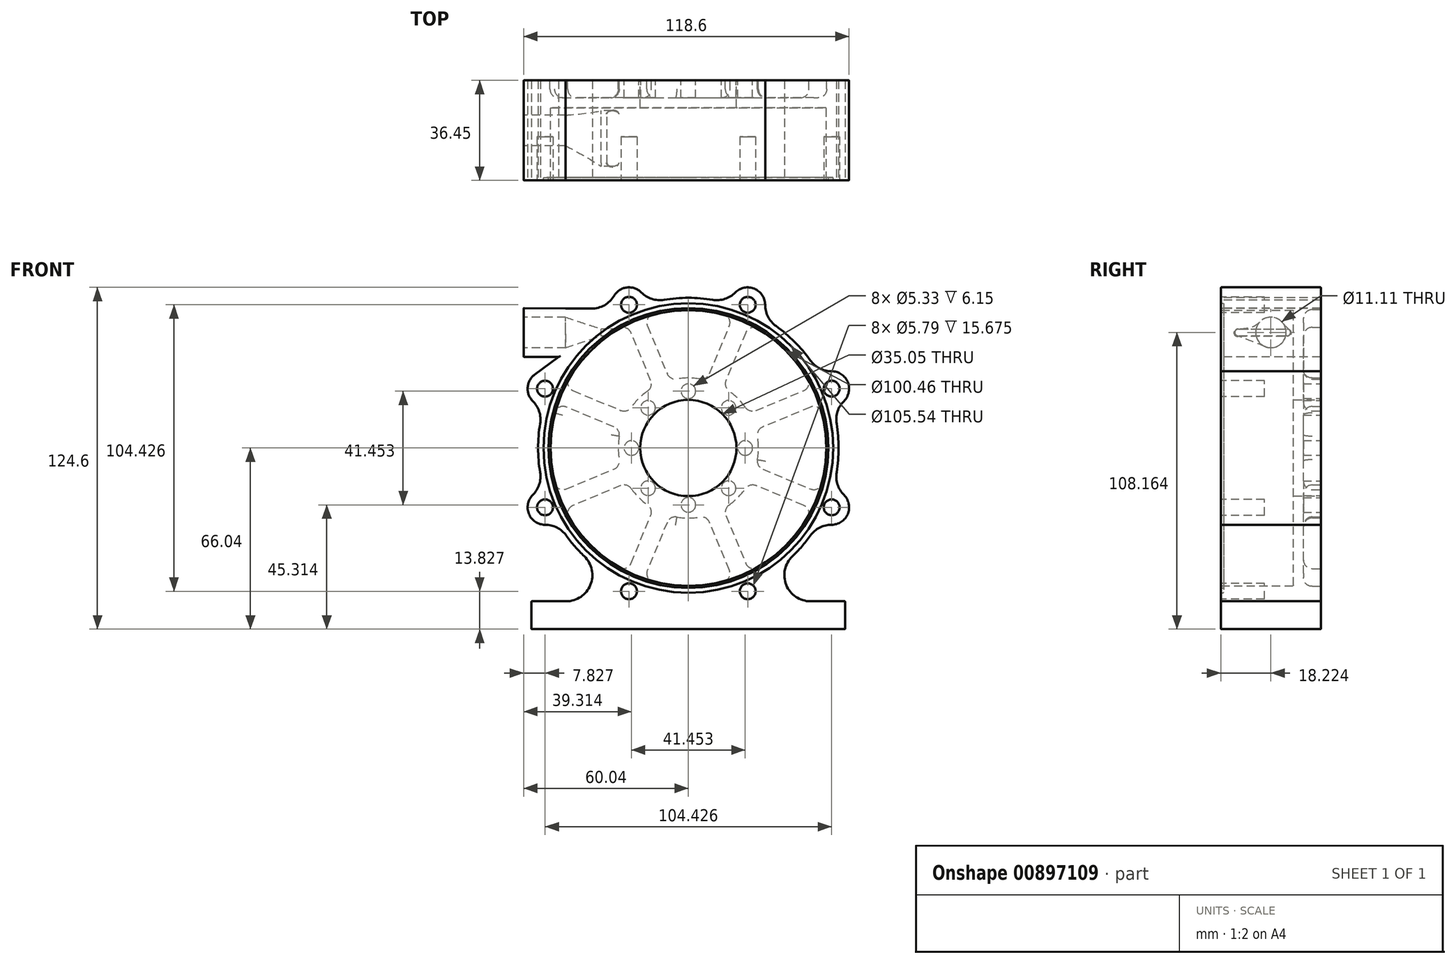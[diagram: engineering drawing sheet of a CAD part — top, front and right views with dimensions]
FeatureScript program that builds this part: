
annotation { "Feature Type Name" : "Feature", "Feature Type Description" : "" }
export const myFeature = defineFeature(function(context is Context, id is Id, definition is map)
    precondition{}
    {
        {
            var Q0;
            Q0=qCreatedBy(makeId("Front.planeOp"),FACE);
            var sketch = newSketch(context, id + "F0", { "sketchPlane" : qUnion([Q0])});
            skCircle(sketch, "E0", {"center": v(0, 0) * mm, "radius": 50.17 * mm, "construction": true});
            skArc(sketch, "E1", {"start": v(54.02, -8.84) * mm, "mid": v(54.74, 0) * mm, "end": v(54.02, 8.84) * mm});
            skCircle(sketch, "E2.cCircle", {"center": v(0, 0) * mm, "radius": 56.52 * mm, "construction": true});
            skLineSegment(sketch, "E2.0", {"start": v(52.21, -21.63) * mm, "end": v(21.63, -52.21) * mm, "construction": true});
            skLineSegment(sketch, "E2.1", {"start": v(21.63, -52.21) * mm, "end": v(-21.63, -52.21) * mm, "construction": true});
            skLineSegment(sketch, "E2.2", {"start": v(-21.63, -52.21) * mm, "end": v(-52.21, -21.63) * mm, "construction": true});
            skLineSegment(sketch, "E2.3", {"start": v(-52.21, -21.63) * mm, "end": v(-52.21, 21.63) * mm, "construction": true});
            skLineSegment(sketch, "E2.4", {"start": v(-52.21, 21.63) * mm, "end": v(-21.63, 52.21) * mm, "construction": true});
            skLineSegment(sketch, "E2.5", {"start": v(-21.63, 52.21) * mm, "end": v(21.63, 52.21) * mm, "construction": true});
            skLineSegment(sketch, "E2.6", {"start": v(21.63, 52.21) * mm, "end": v(52.21, 21.63) * mm, "construction": true});
            skLineSegment(sketch, "E2.7", {"start": v(52.21, 21.63) * mm, "end": v(52.21, -21.63) * mm, "construction": true});
            skArc(sketch, "E3", {"start": v(27.98, 52.2) * mm, "mid": v(24.06, 58.08) * mm, "end": v(17.13, 56.7) * mm});
            skArc(sketch, "E4", {"start": v(56.7, 17.13) * mm, "mid": v(58.08, 24.06) * mm, "end": v(52.2, 27.98) * mm});
            skArc(sketch, "E5", {"start": v(52.2, -27.98) * mm, "mid": v(58.08, -24.06) * mm, "end": v(56.7, -17.13) * mm});
            skArc(sketch, "E6", {"start": v(-56.7, -17.13) * mm, "mid": v(-58.08, -24.06) * mm, "end": v(-52.2, -27.98) * mm});
            skArc(sketch, "E7", {"start": v(-56, 26.73) * mm, "mid": v(-58.55, 22.09) * mm, "end": v(-56.7, 17.13) * mm});
            skArc(sketch, "E8.trimOffspring", {"start": v(44.45, 31.94) * mm, "mid": v(38.7, 38.7) * mm, "end": v(31.94, 44.45) * mm});
            skArc(sketch, "E9.trimOffspring", {"start": v(8.84, 54.02) * mm, "mid": v(0, 54.74) * mm, "end": v(-8.84, 54.02) * mm});
            skArc(sketch, "E10.trimOffspring", {"start": v(-54.02, 8.84) * mm, "mid": v(-54.74, 0) * mm, "end": v(-54.02, -8.84) * mm});
            skArc(sketch, "E11.trimOffspring", {"start": v(-44.45, -31.94) * mm, "mid": v(-41.35, -35.86) * mm, "end": v(-37.9, -39.48) * mm});
            skArc(sketch, "E12.trimOffspring", {"start": v(37.9, -39.48) * mm, "mid": v(41.35, -35.86) * mm, "end": v(44.45, -31.94) * mm});
            skLineSegment(sketch, "E13", {"start": v(-57.15, -55.88) * mm, "end": v(-57.15, -66.04) * mm});
            skLineSegment(sketch, "E14", {"start": v(-57.15, -66.04) * mm, "end": v(57.15, -66.04) * mm});
            skLineSegment(sketch, "E15", {"start": v(57.15, -66.04) * mm, "end": v(57.15, -55.88) * mm});
            skLineSegment(sketch, "E16", {"start": v(57.15, -55.88) * mm, "end": v(44.5, -55.88) * mm});
            skLineSegment(sketch, "E17", {"start": v(-57.15, -55.88) * mm, "end": v(-44.5, -55.88) * mm});
            skPoint(sketch, "E18", {"position": v(0, -66.04) * mm});
            skArc(sketch, "E19", {"start": v(-44.5, -55.88) * mm, "mid": v(-35.67, -49.91) * mm, "end": v(-37.9, -39.48) * mm});
            skArc(sketch, "E20", {"start": v(37.9, -39.48) * mm, "mid": v(35.67, -49.91) * mm, "end": v(44.5, -55.88) * mm});
            skPoint(sketch, "E21.visualSharp", {"position": v(-47.97, -26.36) * mm});
            skArc(sketch, "E21.filletArc", {"start": v(-44.45, -31.94) * mm, "mid": v(-47.85, -29.02) * mm, "end": v(-52.2, -27.98) * mm});
            skPoint(sketch, "E22.visualSharp", {"position": v(-52.56, -15.29) * mm});
            skArc(sketch, "E22.filletArc", {"start": v(-56.7, -17.13) * mm, "mid": v(-54.35, -13.3) * mm, "end": v(-54.02, -8.84) * mm});
            skPoint(sketch, "E23.visualSharp", {"position": v(-52.56, 15.29) * mm});
            skArc(sketch, "E23.filletArc", {"start": v(-54.02, 8.84) * mm, "mid": v(-54.35, 13.3) * mm, "end": v(-56.7, 17.13) * mm});
            skPoint(sketch, "E24.visualSharp", {"position": v(47.97, -26.36) * mm});
            skArc(sketch, "E24.filletArc", {"start": v(52.2, -27.98) * mm, "mid": v(47.85, -29.02) * mm, "end": v(44.45, -31.94) * mm});
            skPoint(sketch, "E25.visualSharp", {"position": v(52.56, -15.29) * mm});
            skArc(sketch, "E25.filletArc", {"start": v(54.02, -8.84) * mm, "mid": v(54.35, -13.3) * mm, "end": v(56.7, -17.13) * mm});
            skPoint(sketch, "E26.visualSharp", {"position": v(52.56, 15.29) * mm});
            skArc(sketch, "E26.filletArc", {"start": v(56.7, 17.13) * mm, "mid": v(54.35, 13.3) * mm, "end": v(54.02, 8.84) * mm});
            skPoint(sketch, "E27.visualSharp", {"position": v(47.97, 26.36) * mm});
            skArc(sketch, "E27.filletArc", {"start": v(44.45, 31.94) * mm, "mid": v(47.85, 29.02) * mm, "end": v(52.2, 27.98) * mm});
            skPoint(sketch, "E28.visualSharp", {"position": v(26.36, 47.97) * mm});
            skArc(sketch, "E28.filletArc", {"start": v(27.98, 52.2) * mm, "mid": v(29.02, 47.85) * mm, "end": v(31.94, 44.45) * mm});
            skPoint(sketch, "E29.visualSharp", {"position": v(15.29, 52.56) * mm});
            skArc(sketch, "E29.filletArc", {"start": v(8.84, 54.02) * mm, "mid": v(13.3, 54.35) * mm, "end": v(17.13, 56.7) * mm});
            skPoint(sketch, "E30.visualSharp", {"position": v(-15.29, 52.56) * mm});
            skLineSegment(sketch, "E31", {"start": v(-35.27, 50.8) * mm, "end": v(-44.8, 50.8) * mm});
            skArc(sketch, "E32", {"start": v(-17.13, 56.7) * mm, "mid": v(-22.41, 58.51) * mm, "end": v(-27.09, 55.46) * mm});
            skArc(sketch, "E33.filletArc", {"start": v(-17.13, 56.7) * mm, "mid": v(-13.3, 54.35) * mm, "end": v(-8.84, 54.02) * mm});
            skPoint(sketch, "E34.visualSharp", {"position": v(-27.82, 50.8) * mm});
            skArc(sketch, "E34.filletArc", {"start": v(-35.27, 50.8) * mm, "mid": v(-30.56, 52.05) * mm, "end": v(-27.09, 55.46) * mm});
            skLineSegment(sketch, "E35", {"start": v(-47.22, 33.23) * mm, "end": v(-56, 26.73) * mm});
            skLineSegment(sketch, "E36", {"start": v(-44.8, 50.8) * mm, "end": v(-60.04, 51.01) * mm});
            skLineSegment(sketch, "E37", {"start": v(-60.04, 51.01) * mm, "end": v(-60.04, 33.23) * mm});
            skLineSegment(sketch, "E38", {"start": v(-60.04, 33.23) * mm, "end": v(-47.22, 33.23) * mm});
            skSolve(sketch);
        }
        {
            var Q0;
            Q0=qSketchRegion(id+"F0",true);
            extrude(context, id + "F1", {"entities" : qUnion([Q0]), "oppositeDirection" : true, "depth" : 36.45 * mm});
        }
        {
            var Q0;
            Q0=qCreatedBy(makeId("Right.planeOp"),FACE);
            var sketch = newSketch(context, id + "F2", { "sketchPlane" : qUnion([Q0])});
            skLineSegment(sketch, "E39", {"start": v(0, 0) * mm, "end": v(0, 50.23) * mm});
            skLineSegment(sketch, "E40", {"start": v(26.42, 50.23) * mm, "end": v(0, 50.23) * mm});
            skLineSegment(sketch, "E41", {"start": v(26.42, 50.23) * mm, "end": v(26.42, 17.53) * mm});
            skLineSegment(sketch, "E42", {"start": v(36.45, 17.53) * mm, "end": v(26.42, 17.53) * mm});
            skLineSegment(sketch, "E43", {"start": v(36.45, 17.53) * mm, "end": v(36.45, 0) * mm});
            skLineSegment(sketch, "E44", {"start": v(0, 0) * mm, "end": v(36.45, 0) * mm});
            skLineSegment(sketch, "E45.bottom", {"start": v(1.02, 51) * mm, "end": v(0, 51) * mm});
            skLineSegment(sketch, "E45.top", {"start": v(1.02, 52.77) * mm, "end": v(0, 52.77) * mm});
            skLineSegment(sketch, "E45.left", {"start": v(0, 51) * mm, "end": v(0, 52.77) * mm});
            skLineSegment(sketch, "E45.right", {"start": v(1.02, 51) * mm, "end": v(1.02, 52.77) * mm});
            skSolve(sketch);
        }
        {
            var Q0;
            Q0=qSketchRegion(id+"F2",true);
            var Q1;
            Q1=sQuery(id+"F2.wireOp",EDGE,"E44");
            revolve(context, id + "F3", {"operationType" : NewBodyOperationType.REMOVE, "entities" : qUnion([Q0]), "axis" : qUnion([Q1]), "revolveType" : RevolveType.FULL, "oppositeDirection" : true});
        }
        {
            var Q0;
            Q0=makeQuery(id+"F1.opExtrude","CAP_FACE",FACE,{"disambiguationData":[OSD([sQuery(id+"F0.wireOp",EDGE,"E1"),sQuery(id+"F0.wireOp",EDGE,"E3"),sQuery(id+"F0.wireOp",EDGE,"E4"),sQuery(id+"F0.wireOp",EDGE,"E5"),sQuery(id+"F0.wireOp",EDGE,"E6"),sQuery(id+"F0.wireOp",EDGE,"E7"),sQuery(id+"F0.wireOp",EDGE,"E8.trimOffspring"),sQuery(id+"F0.wireOp",EDGE,"E9.trimOffspring"),sQuery(id+"F0.wireOp",EDGE,"E10.trimOffspring"),sQuery(id+"F0.wireOp",EDGE,"E11.trimOffspring"),sQuery(id+"F0.wireOp",EDGE,"E12.trimOffspring"),sQuery(id+"F0.wireOp",EDGE,"E13"),sQuery(id+"F0.wireOp",EDGE,"E14"),sQuery(id+"F0.wireOp",EDGE,"E15"),sQuery(id+"F0.wireOp",EDGE,"E16"),sQuery(id+"F0.wireOp",EDGE,"E17"),sQuery(id+"F0.wireOp",EDGE,"E19"),sQuery(id+"F0.wireOp",EDGE,"E20"),sQuery(id+"F0.wireOp",EDGE,"E21.filletArc"),sQuery(id+"F0.wireOp",EDGE,"E22.filletArc"),sQuery(id+"F0.wireOp",EDGE,"E23.filletArc"),sQuery(id+"F0.wireOp",EDGE,"E24.filletArc"),sQuery(id+"F0.wireOp",EDGE,"E25.filletArc"),sQuery(id+"F0.wireOp",EDGE,"E26.filletArc"),sQuery(id+"F0.wireOp",EDGE,"E27.filletArc"),sQuery(id+"F0.wireOp",EDGE,"E28.filletArc"),sQuery(id+"F0.wireOp",EDGE,"E29.filletArc"),sQuery(id+"F0.wireOp",EDGE,"E31"),sQuery(id+"F0.wireOp",EDGE,"kHr8fFUD-4EFk-nJZE-7JVT-0WPmz8yTTr2E"),sQuery(id+"F0.wireOp",EDGE,"E32"),sQuery(id+"F0.wireOp",EDGE,"E33.filletArc"),sQuery(id+"F0.wireOp",EDGE,"E34.filletArc"),sQuery(id+"F0.wireOp",EDGE,"fBgQRkSS-CIUt-JJdx-RIVp-XrYWp9c1mPRc"),sQuery(id+"F0.wireOp",EDGE,"E35")])],"isStart":false});
            var sketch = newSketch(context, id + "F4", { "sketchPlane" : qUnion([Q0])});
            skPoint(sketch, "E46.center", {"position": v(0, 0) * mm});
            skArc(sketch, "E47", {"start": v(4.25, 25.17) * mm, "mid": v(0, 25.53) * mm, "end": v(-4.25, 25.17) * mm});
            skLineSegment(sketch, "E48", {"start": v(0, 0) * mm, "end": v(24.06, 58.08) * mm, "construction": true});
            skLineSegment(sketch, "E49", {"start": v(0, 0) * mm, "end": v(0, 17.53) * mm, "construction": true});
            skArc(sketch, "E50", {"start": v(12.8, 48.77) * mm, "mid": v(0, 50.42) * mm, "end": v(-12.8, 48.77) * mm});
            skLineSegment(sketch, "E51", {"start": v(14.92, 44.48) * mm, "end": v(7.71, 27.09) * mm});
            skLineSegment(sketch, "E52", {"start": v(-7.71, 27.09) * mm, "end": v(-14.92, 44.48) * mm});
            skPoint(sketch, "E53.visualSharp", {"position": v(-16.26, 47.72) * mm});
            skArc(sketch, "E53.filletArc", {"start": v(-12.8, 48.77) * mm, "mid": v(-14.83, 47.1) * mm, "end": v(-14.92, 44.48) * mm});
            skPoint(sketch, "E54.visualSharp", {"position": v(16.26, 47.72) * mm});
            skArc(sketch, "E54.filletArc", {"start": v(14.92, 44.48) * mm, "mid": v(14.83, 47.1) * mm, "end": v(12.8, 48.77) * mm});
            skPoint(sketch, "E55.visualSharp", {"position": v(6.7, 24.63) * mm});
            skArc(sketch, "E55.filletArc", {"start": v(4.25, 25.17) * mm, "mid": v(6.32, 25.52) * mm, "end": v(7.71, 27.09) * mm});
            skPoint(sketch, "E56.visualSharp", {"position": v(-6.7, 24.63) * mm});
            skArc(sketch, "E56.filletArc", {"start": v(-7.71, 27.09) * mm, "mid": v(-6.32, 25.52) * mm, "end": v(-4.25, 25.17) * mm});
            skArc(sketch, "E57.1.0", {"start": v(-43.53, 25.44) * mm, "mid": v(-43.8, 22.82) * mm, "end": v(-42, 20.9) * mm});
            skLineSegment(sketch, "E57.1.1", {"start": v(-24.6, 13.7) * mm, "end": v(-42, 20.9) * mm});
            skArc(sketch, "E57.1.2", {"start": v(-14.8, 20.8) * mm, "mid": v(-18.05, 18.05) * mm, "end": v(-20.8, 14.8) * mm});
            skArc(sketch, "E57.1.3", {"start": v(-24.6, 13.7) * mm, "mid": v(-22.51, 13.58) * mm, "end": v(-20.8, 14.8) * mm});
            skArc(sketch, "E57.1.4", {"start": v(-14.8, 20.8) * mm, "mid": v(-13.58, 22.51) * mm, "end": v(-13.7, 24.6) * mm});
            skLineSegment(sketch, "E57.1.5", {"start": v(-20.9, 42) * mm, "end": v(-13.7, 24.6) * mm});
            skArc(sketch, "E57.1.6", {"start": v(-20.9, 42) * mm, "mid": v(-22.82, 43.8) * mm, "end": v(-25.44, 43.53) * mm});
            skArc(sketch, "E57.1.7", {"start": v(-25.44, 43.53) * mm, "mid": v(-35.65, 35.65) * mm, "end": v(-43.53, 25.44) * mm});
            skArc(sketch, "E57.2.0", {"start": v(-48.77, -12.8) * mm, "mid": v(-47.1, -14.83) * mm, "end": v(-44.48, -14.92) * mm});
            skLineSegment(sketch, "E57.2.1", {"start": v(-27.09, -7.71) * mm, "end": v(-44.48, -14.92) * mm});
            skArc(sketch, "E57.2.2", {"start": v(-25.17, 4.25) * mm, "mid": v(-25.53, 0) * mm, "end": v(-25.17, -4.25) * mm});
            skArc(sketch, "E57.2.3", {"start": v(-27.09, -7.71) * mm, "mid": v(-25.52, -6.32) * mm, "end": v(-25.17, -4.25) * mm});
            skArc(sketch, "E57.2.4", {"start": v(-25.17, 4.25) * mm, "mid": v(-25.52, 6.32) * mm, "end": v(-27.09, 7.71) * mm});
            skLineSegment(sketch, "E57.2.5", {"start": v(-44.48, 14.92) * mm, "end": v(-27.09, 7.71) * mm});
            skArc(sketch, "E57.2.6", {"start": v(-44.48, 14.92) * mm, "mid": v(-47.1, 14.83) * mm, "end": v(-48.77, 12.8) * mm});
            skArc(sketch, "E57.2.7", {"start": v(-48.77, 12.8) * mm, "mid": v(-50.42, 0) * mm, "end": v(-48.77, -12.8) * mm});
            skArc(sketch, "E57.3.0", {"start": v(-25.44, -43.53) * mm, "mid": v(-22.82, -43.8) * mm, "end": v(-20.9, -42) * mm});
            skLineSegment(sketch, "E57.3.1", {"start": v(-13.7, -24.6) * mm, "end": v(-20.9, -42) * mm});
            skArc(sketch, "E57.3.2", {"start": v(-20.8, -14.8) * mm, "mid": v(-18.05, -18.05) * mm, "end": v(-14.8, -20.8) * mm});
            skArc(sketch, "E57.3.3", {"start": v(-13.7, -24.6) * mm, "mid": v(-13.58, -22.51) * mm, "end": v(-14.8, -20.8) * mm});
            skArc(sketch, "E57.3.4", {"start": v(-20.8, -14.8) * mm, "mid": v(-22.51, -13.58) * mm, "end": v(-24.6, -13.7) * mm});
            skLineSegment(sketch, "E57.3.5", {"start": v(-42, -20.9) * mm, "end": v(-24.6, -13.7) * mm});
            skArc(sketch, "E57.3.6", {"start": v(-42, -20.9) * mm, "mid": v(-43.8, -22.82) * mm, "end": v(-43.53, -25.44) * mm});
            skArc(sketch, "E57.3.7", {"start": v(-43.53, -25.44) * mm, "mid": v(-35.65, -35.65) * mm, "end": v(-25.44, -43.53) * mm});
            skArc(sketch, "E57.4.0", {"start": v(12.8, -48.77) * mm, "mid": v(14.83, -47.1) * mm, "end": v(14.92, -44.48) * mm});
            skLineSegment(sketch, "E57.4.1", {"start": v(7.71, -27.09) * mm, "end": v(14.92, -44.48) * mm});
            skArc(sketch, "E57.4.2", {"start": v(-4.25, -25.17) * mm, "mid": v(0, -25.53) * mm, "end": v(4.25, -25.17) * mm});
            skArc(sketch, "E57.4.3", {"start": v(7.71, -27.09) * mm, "mid": v(6.32, -25.52) * mm, "end": v(4.25, -25.17) * mm});
            skArc(sketch, "E57.4.4", {"start": v(-4.25, -25.17) * mm, "mid": v(-6.32, -25.52) * mm, "end": v(-7.71, -27.09) * mm});
            skLineSegment(sketch, "E57.4.5", {"start": v(-14.92, -44.48) * mm, "end": v(-7.71, -27.09) * mm});
            skArc(sketch, "E57.4.6", {"start": v(-14.92, -44.48) * mm, "mid": v(-14.83, -47.1) * mm, "end": v(-12.8, -48.77) * mm});
            skArc(sketch, "E57.4.7", {"start": v(-12.8, -48.77) * mm, "mid": v(0, -50.42) * mm, "end": v(12.8, -48.77) * mm});
            skArc(sketch, "E57.5.0", {"start": v(43.53, -25.44) * mm, "mid": v(43.8, -22.82) * mm, "end": v(42, -20.9) * mm});
            skLineSegment(sketch, "E57.5.1", {"start": v(24.6, -13.7) * mm, "end": v(42, -20.9) * mm});
            skArc(sketch, "E57.5.2", {"start": v(14.8, -20.8) * mm, "mid": v(18.05, -18.05) * mm, "end": v(20.8, -14.8) * mm});
            skArc(sketch, "E57.5.3", {"start": v(24.6, -13.7) * mm, "mid": v(22.51, -13.58) * mm, "end": v(20.8, -14.8) * mm});
            skArc(sketch, "E57.5.4", {"start": v(14.8, -20.8) * mm, "mid": v(13.58, -22.51) * mm, "end": v(13.7, -24.6) * mm});
            skLineSegment(sketch, "E57.5.5", {"start": v(20.9, -42) * mm, "end": v(13.7, -24.6) * mm});
            skArc(sketch, "E57.5.6", {"start": v(20.9, -42) * mm, "mid": v(22.82, -43.8) * mm, "end": v(25.44, -43.53) * mm});
            skArc(sketch, "E57.5.7", {"start": v(25.44, -43.53) * mm, "mid": v(35.65, -35.65) * mm, "end": v(43.53, -25.44) * mm});
            skArc(sketch, "E57.6.0", {"start": v(48.77, 12.8) * mm, "mid": v(47.1, 14.83) * mm, "end": v(44.48, 14.92) * mm});
            skLineSegment(sketch, "E57.6.1", {"start": v(27.09, 7.71) * mm, "end": v(44.48, 14.92) * mm});
            skArc(sketch, "E57.6.2", {"start": v(25.17, -4.25) * mm, "mid": v(25.53, 0) * mm, "end": v(25.17, 4.25) * mm});
            skArc(sketch, "E57.6.3", {"start": v(27.09, 7.71) * mm, "mid": v(25.52, 6.32) * mm, "end": v(25.17, 4.25) * mm});
            skArc(sketch, "E57.6.4", {"start": v(25.17, -4.25) * mm, "mid": v(25.52, -6.32) * mm, "end": v(27.09, -7.71) * mm});
            skLineSegment(sketch, "E57.6.5", {"start": v(44.48, -14.92) * mm, "end": v(27.09, -7.71) * mm});
            skArc(sketch, "E57.6.6", {"start": v(44.48, -14.92) * mm, "mid": v(47.1, -14.83) * mm, "end": v(48.77, -12.8) * mm});
            skArc(sketch, "E57.6.7", {"start": v(48.77, -12.8) * mm, "mid": v(50.42, 0) * mm, "end": v(48.77, 12.8) * mm});
            skArc(sketch, "E57.7.0", {"start": v(25.44, 43.53) * mm, "mid": v(22.82, 43.8) * mm, "end": v(20.9, 42) * mm});
            skLineSegment(sketch, "E57.7.1", {"start": v(13.7, 24.6) * mm, "end": v(20.9, 42) * mm});
            skArc(sketch, "E57.7.2", {"start": v(20.8, 14.8) * mm, "mid": v(18.05, 18.05) * mm, "end": v(14.8, 20.8) * mm});
            skArc(sketch, "E57.7.3", {"start": v(13.7, 24.6) * mm, "mid": v(13.58, 22.51) * mm, "end": v(14.8, 20.8) * mm});
            skArc(sketch, "E57.7.4", {"start": v(20.8, 14.8) * mm, "mid": v(22.51, 13.58) * mm, "end": v(24.6, 13.7) * mm});
            skLineSegment(sketch, "E57.7.5", {"start": v(42, 20.9) * mm, "end": v(24.6, 13.7) * mm});
            skArc(sketch, "E57.7.6", {"start": v(42, 20.9) * mm, "mid": v(43.8, 22.82) * mm, "end": v(43.53, 25.44) * mm});
            skArc(sketch, "E57.7.7", {"start": v(43.53, 25.44) * mm, "mid": v(35.65, 35.65) * mm, "end": v(25.44, 43.53) * mm});
            skSolve(sketch);
        }
        {
            var Q0;
            Q0=qSketchRegion(id+"F4",true);
            extrude(context, id + "F5", {"entities" : qUnion([Q0]), "operationType" : NewBodyOperationType.REMOVE, "oppositeDirection" : true, "depth" : 6.35 * mm});
        }
        {
            var Q0;
            Q0=makeQuery(id+"F5.boolean.opBoolean","COPY",FACE,{"derivedFrom":makeQuery(id+"F5.opExtrude","CAP_FACE",FACE,{"disambiguationData":[OSD([sQuery(id+"F4.wireOp",EDGE,"E47"),sQuery(id+"F4.wireOp",EDGE,"E50"),sQuery(id+"F4.wireOp",EDGE,"E51"),sQuery(id+"F4.wireOp",EDGE,"E52"),sQuery(id+"F4.wireOp",EDGE,"E53.filletArc"),sQuery(id+"F4.wireOp",EDGE,"E54.filletArc"),sQuery(id+"F4.wireOp",EDGE,"E55.filletArc"),sQuery(id+"F4.wireOp",EDGE,"E56.filletArc")])],"isStart":false})});
            var Q1;
            Q1=makeQuery(id+"F5.boolean.opBoolean","COPY",FACE,{"derivedFrom":makeQuery(id+"F5.opExtrude","CAP_FACE",FACE,{"disambiguationData":[OSD([sQuery(id+"F4.wireOp",EDGE,"E57.7.0"),sQuery(id+"F4.wireOp",EDGE,"E57.7.1"),sQuery(id+"F4.wireOp",EDGE,"E57.7.2"),sQuery(id+"F4.wireOp",EDGE,"E57.7.3"),sQuery(id+"F4.wireOp",EDGE,"E57.7.4"),sQuery(id+"F4.wireOp",EDGE,"E57.7.5"),sQuery(id+"F4.wireOp",EDGE,"E57.7.6"),sQuery(id+"F4.wireOp",EDGE,"E57.7.7")])],"isStart":false})});
            var Q2;
            Q2=makeQuery(id+"F5.boolean.opBoolean","COPY",FACE,{"derivedFrom":makeQuery(id+"F5.opExtrude","CAP_FACE",FACE,{"disambiguationData":[OSD([sQuery(id+"F4.wireOp",EDGE,"E57.6.0"),sQuery(id+"F4.wireOp",EDGE,"E57.6.1"),sQuery(id+"F4.wireOp",EDGE,"E57.6.2"),sQuery(id+"F4.wireOp",EDGE,"E57.6.3"),sQuery(id+"F4.wireOp",EDGE,"E57.6.4"),sQuery(id+"F4.wireOp",EDGE,"E57.6.5"),sQuery(id+"F4.wireOp",EDGE,"E57.6.6"),sQuery(id+"F4.wireOp",EDGE,"E57.6.7")])],"isStart":false})});
            var Q3;
            Q3=makeQuery(id+"F5.boolean.opBoolean","COPY",FACE,{"derivedFrom":makeQuery(id+"F5.opExtrude","CAP_FACE",FACE,{"disambiguationData":[OSD([sQuery(id+"F4.wireOp",EDGE,"E57.5.0"),sQuery(id+"F4.wireOp",EDGE,"E57.5.1"),sQuery(id+"F4.wireOp",EDGE,"E57.5.2"),sQuery(id+"F4.wireOp",EDGE,"E57.5.3"),sQuery(id+"F4.wireOp",EDGE,"E57.5.4"),sQuery(id+"F4.wireOp",EDGE,"E57.5.5"),sQuery(id+"F4.wireOp",EDGE,"E57.5.6"),sQuery(id+"F4.wireOp",EDGE,"E57.5.7")])],"isStart":false})});
            var Q4;
            Q4=makeQuery(id+"F5.boolean.opBoolean","COPY",FACE,{"derivedFrom":makeQuery(id+"F5.opExtrude","CAP_FACE",FACE,{"disambiguationData":[OSD([sQuery(id+"F4.wireOp",EDGE,"E57.4.0"),sQuery(id+"F4.wireOp",EDGE,"E57.4.1"),sQuery(id+"F4.wireOp",EDGE,"E57.4.2"),sQuery(id+"F4.wireOp",EDGE,"E57.4.3"),sQuery(id+"F4.wireOp",EDGE,"E57.4.4"),sQuery(id+"F4.wireOp",EDGE,"E57.4.5"),sQuery(id+"F4.wireOp",EDGE,"E57.4.6"),sQuery(id+"F4.wireOp",EDGE,"E57.4.7")])],"isStart":false})});
            var Q5;
            Q5=makeQuery(id+"F5.boolean.opBoolean","COPY",FACE,{"derivedFrom":makeQuery(id+"F5.opExtrude","CAP_FACE",FACE,{"disambiguationData":[OSD([sQuery(id+"F4.wireOp",EDGE,"E57.3.0"),sQuery(id+"F4.wireOp",EDGE,"E57.3.1"),sQuery(id+"F4.wireOp",EDGE,"E57.3.2"),sQuery(id+"F4.wireOp",EDGE,"E57.3.3"),sQuery(id+"F4.wireOp",EDGE,"E57.3.4"),sQuery(id+"F4.wireOp",EDGE,"E57.3.5"),sQuery(id+"F4.wireOp",EDGE,"E57.3.6"),sQuery(id+"F4.wireOp",EDGE,"E57.3.7")])],"isStart":false})});
            var Q6;
            Q6=makeQuery(id+"F5.boolean.opBoolean","COPY",FACE,{"derivedFrom":makeQuery(id+"F5.opExtrude","CAP_FACE",FACE,{"disambiguationData":[OSD([sQuery(id+"F4.wireOp",EDGE,"E57.2.0"),sQuery(id+"F4.wireOp",EDGE,"E57.2.1"),sQuery(id+"F4.wireOp",EDGE,"E57.2.2"),sQuery(id+"F4.wireOp",EDGE,"E57.2.3"),sQuery(id+"F4.wireOp",EDGE,"E57.2.4"),sQuery(id+"F4.wireOp",EDGE,"E57.2.5"),sQuery(id+"F4.wireOp",EDGE,"E57.2.6"),sQuery(id+"F4.wireOp",EDGE,"E57.2.7")])],"isStart":false})});
            var Q7;
            Q7=makeQuery(id+"F5.boolean.opBoolean","COPY",FACE,{"derivedFrom":makeQuery(id+"F5.opExtrude","CAP_FACE",FACE,{"disambiguationData":[OSD([sQuery(id+"F4.wireOp",EDGE,"E57.1.0"),sQuery(id+"F4.wireOp",EDGE,"E57.1.1"),sQuery(id+"F4.wireOp",EDGE,"E57.1.2"),sQuery(id+"F4.wireOp",EDGE,"E57.1.3"),sQuery(id+"F4.wireOp",EDGE,"E57.1.4"),sQuery(id+"F4.wireOp",EDGE,"E57.1.5"),sQuery(id+"F4.wireOp",EDGE,"E57.1.6"),sQuery(id+"F4.wireOp",EDGE,"E57.1.7")])],"isStart":false})});
            fillet(context, id + "F6", {"entities" : qUnion([Q0, Q1, Q2, Q3, Q4, Q5, Q6, Q7]), "radius" : 3.17 * mm, "tangentPropagation" : true, "allowEdgeOverflow" : false});
        }
        {
            var Q0;
            Q0=makeQuery(id+"F1.opExtrude","CAP_FACE",FACE,{"disambiguationData":[OSD([sQuery(id+"F0.wireOp",EDGE,"E1"),sQuery(id+"F0.wireOp",EDGE,"E3"),sQuery(id+"F0.wireOp",EDGE,"E4"),sQuery(id+"F0.wireOp",EDGE,"E5"),sQuery(id+"F0.wireOp",EDGE,"E6"),sQuery(id+"F0.wireOp",EDGE,"E7"),sQuery(id+"F0.wireOp",EDGE,"E8.trimOffspring"),sQuery(id+"F0.wireOp",EDGE,"E9.trimOffspring"),sQuery(id+"F0.wireOp",EDGE,"E10.trimOffspring"),sQuery(id+"F0.wireOp",EDGE,"E11.trimOffspring"),sQuery(id+"F0.wireOp",EDGE,"E12.trimOffspring"),sQuery(id+"F0.wireOp",EDGE,"E13"),sQuery(id+"F0.wireOp",EDGE,"E14"),sQuery(id+"F0.wireOp",EDGE,"E15"),sQuery(id+"F0.wireOp",EDGE,"E16"),sQuery(id+"F0.wireOp",EDGE,"E17"),sQuery(id+"F0.wireOp",EDGE,"E19"),sQuery(id+"F0.wireOp",EDGE,"E20"),sQuery(id+"F0.wireOp",EDGE,"E21.filletArc"),sQuery(id+"F0.wireOp",EDGE,"E22.filletArc"),sQuery(id+"F0.wireOp",EDGE,"E23.filletArc"),sQuery(id+"F0.wireOp",EDGE,"E24.filletArc"),sQuery(id+"F0.wireOp",EDGE,"E25.filletArc"),sQuery(id+"F0.wireOp",EDGE,"E26.filletArc"),sQuery(id+"F0.wireOp",EDGE,"E27.filletArc"),sQuery(id+"F0.wireOp",EDGE,"E28.filletArc"),sQuery(id+"F0.wireOp",EDGE,"E29.filletArc"),sQuery(id+"F0.wireOp",EDGE,"E31"),sQuery(id+"F0.wireOp",EDGE,"kHr8fFUD-4EFk-nJZE-7JVT-0WPmz8yTTr2E"),sQuery(id+"F0.wireOp",EDGE,"E32"),sQuery(id+"F0.wireOp",EDGE,"E33.filletArc"),sQuery(id+"F0.wireOp",EDGE,"E34.filletArc"),sQuery(id+"F0.wireOp",EDGE,"fBgQRkSS-CIUt-JJdx-RIVp-XrYWp9c1mPRc"),sQuery(id+"F0.wireOp",EDGE,"E35")])],"isStart":false});
            var sketch = newSketch(context, id + "F7", { "sketchPlane" : qUnion([Q0])});
            skCircle(sketch, "E58", {"center": v(0, 20.73) * mm, "radius": 2.67 * mm});
            skCircle(sketch, "E59.1.0", {"center": v(-14.66, 14.66) * mm, "radius": 2.67 * mm});
            skCircle(sketch, "E59.2.0", {"center": v(-20.73, 0) * mm, "radius": 2.67 * mm});
            skCircle(sketch, "E59.3.0", {"center": v(-14.66, -14.66) * mm, "radius": 2.67 * mm});
            skCircle(sketch, "E59.4.0", {"center": v(0, -20.73) * mm, "radius": 2.67 * mm});
            skCircle(sketch, "E59.5.0", {"center": v(14.66, -14.66) * mm, "radius": 2.67 * mm});
            skCircle(sketch, "E59.6.0", {"center": v(20.73, 0) * mm, "radius": 2.67 * mm});
            skCircle(sketch, "E59.7.0", {"center": v(14.66, 14.66) * mm, "radius": 2.67 * mm});
            skPoint(sketch, "E59.center", {"position": v(0, 0) * mm});
            skSolve(sketch);
        }
        {
            var Q0;
            Q0=qSketchRegion(id+"F7",true);
            extrude(context, id + "F8", {"entities" : qUnion([Q0]), "operationType" : NewBodyOperationType.REMOVE, "oppositeDirection" : true, "depth" : 6.35 * mm});
        }
        {
            var Q0;
            Q0=qCreatedBy(makeId("Front.planeOp"),FACE);
            var sketch = newSketch(context, id + "F9", { "sketchPlane" : qUnion([Q0])});
            skCircle(sketch, "E60", {"center": v(21.63, 52.21) * mm, "radius": 2.9 * mm});
            skCircle(sketch, "E61.1.0", {"center": v(-21.63, 52.21) * mm, "radius": 2.9 * mm});
            skCircle(sketch, "E61.2.0", {"center": v(-52.21, 21.63) * mm, "radius": 2.9 * mm});
            skCircle(sketch, "E61.3.0", {"center": v(-52.21, -21.63) * mm, "radius": 2.9 * mm});
            skCircle(sketch, "E61.4.0", {"center": v(-21.63, -52.21) * mm, "radius": 2.9 * mm});
            skCircle(sketch, "E61.5.0", {"center": v(21.63, -52.21) * mm, "radius": 2.9 * mm});
            skCircle(sketch, "E61.6.0", {"center": v(52.21, -21.63) * mm, "radius": 2.9 * mm});
            skCircle(sketch, "E61.7.0", {"center": v(52.21, 21.63) * mm, "radius": 2.9 * mm});
            skPoint(sketch, "E61.center", {"position": v(0, 0) * mm});
            skSolve(sketch);
        }
        {
            var Q0;
            Q0=qSketchRegion(id+"F9",true);
            extrude(context, id + "F10", {"entities" : qUnion([Q0]), "operationType" : NewBodyOperationType.REMOVE, "oppositeDirection" : true, "depth" : 15.88 * mm});
        }
        {
            var Q0;
            Q0=makeQuery(id+"F1.opExtrude","SWEPT_FACE",FACE,{"disambiguationData":[OSD([sQuery(id+"F0.wireOp",EDGE,"E37")])]});
            var sketch = newSketch(context, id + "F11", { "sketchPlane" : qUnion([Q0])});
            skCircle(sketch, "E62", {"center": v(-18.22, 42.12) * mm, "radius": 5.56 * mm});
            skPoint(sketch, "E63", {"position": v(-18.22, 51.01) * mm});
            skPoint(sketch, "E64", {"position": v(0, 42.12) * mm});
            skSolve(sketch);
        }
        {
            var Q0;
            Q0=qSketchRegion(id+"F11",true);
            extrude(context, id + "F12", {"entities" : qUnion([Q0]), "operationType" : NewBodyOperationType.REMOVE, "oppositeDirection" : true, "depth" : 15.24 * mm});
        }
        {
            var Q0;
            Q0=qCreatedBy(makeId("Right.planeOp"),FACE);
            cPlane(context, id + "F13", {"entities" : qUnion([Q0]), "cplaneType" : CPlaneType.OFFSET, "offset" : 31.75 * mm, "oppositeDirection" : true, "width" : 152.4 * mm, "height" : 152.4 * mm});
        }
        {
            var Q0;
            Q0=qCreatedBy(id+"F13.planeOp",FACE);
            var sketch = newSketch(context, id + "F14", { "sketchPlane" : qUnion([Q0])});
            skLineSegment(sketch, "E65", {"start": v(6.35, 43.4) * mm, "end": v(24.13, 43.4) * mm});
            skLineSegment(sketch, "E66", {"start": v(24.13, 40.85) * mm, "end": v(6.35, 40.85) * mm});
            skArc(sketch, "E67", {"start": v(24.13, 40.85) * mm, "mid": v(25.4, 42.12) * mm, "end": v(24.13, 43.4) * mm});
            skArc(sketch, "E68", {"start": v(6.35, 43.4) * mm, "mid": v(5.08, 42.12) * mm, "end": v(6.35, 40.85) * mm});
            skPoint(sketch, "E69", {"position": v(18.22, 42.12) * mm});
            skSolve(sketch);
        }
        {
            var Q0;
            Q0=makeQuery(id+"F12.boolean.opBoolean","COPY",FACE,{"derivedFrom":makeQuery(id+"F12.opExtrude","CAP_FACE",FACE,{"disambiguationData":[OSD([sQuery(id+"F11.wireOp",EDGE,"E62")])],"isStart":false})});
            var sketch = newSketch(context, id + "F15", { "sketchPlane" : qUnion([Q0])});
            skCircle(sketch, "E70", {"center": v(-18.22, 42.12) * mm, "radius": 5.56 * mm});
            skSolve(sketch);
        }
        {
            var Q1;
            Q1=qSketchRegion(id+"F14",true);
            var Q2;
            Q2=qSketchRegion(id+"F15",true);
            loft(context, id + "F16", {"operationType" : NewBodyOperationType.REMOVE, "sheetProfilesArray" : [{ "sheetProfileEntities" : qUnion([Q1]) }, { "sheetProfileEntities" : qUnion([Q2]) }]});
        }
        {
            var Q0;
            Q0=qSketchRegion(id+"F14",true);
            extrude(context, id + "F17", {"entities" : qUnion([Q0]), "operationType" : NewBodyOperationType.REMOVE, "depth" : 25.4 * mm});
        }
        {
            var Q0;
            {var subQ0=sQuery(id+"F0.wireOp",EDGE,"E23.filletArc");var subQ1=sQuery(id+"F0.wireOp",EDGE,"E22.filletArc");var subQ2=sQuery(id+"F0.wireOp",EDGE,"E21.filletArc");var subQ3=sQuery(id+"F0.wireOp",EDGE,"E20");var subQ4=sQuery(id+"F0.wireOp",EDGE,"E19");var subQ5=sQuery(id+"F0.wireOp",EDGE,"E17");var subQ6=sQuery(id+"F0.wireOp",EDGE,"E16");var subQ7=sQuery(id+"F0.wireOp",EDGE,"E15");var subQ8=sQuery(id+"F0.wireOp",EDGE,"E14");var subQ9=sQuery(id+"F0.wireOp",EDGE,"E13");var subQ10=sQuery(id+"F0.wireOp",EDGE,"E12.trimOffspring");var subQ11=sQuery(id+"F0.wireOp",EDGE,"E4");var subQ12=sQuery(id+"F0.wireOp",EDGE,"E3");var subQ13=sQuery(id+"F0.wireOp",EDGE,"E5");var subQ14=sQuery(id+"F0.wireOp",EDGE,"E24.filletArc");var subQ15=sQuery(id+"F0.wireOp",EDGE,"E1");var subQ16=sQuery(id+"F0.wireOp",EDGE,"E11.trimOffspring");var subQ17=sQuery(id+"F0.wireOp",EDGE,"E6");var subQ18=sQuery(id+"F0.wireOp",EDGE,"E7");var subQ19=sQuery(id+"F0.wireOp",EDGE,"E8.trimOffspring");var subQ20=sQuery(id+"F0.wireOp",EDGE,"E9.trimOffspring");var subQ21=sQuery(id+"F0.wireOp",EDGE,"E10.trimOffspring");var subQ22=sQuery(id+"F0.wireOp",EDGE,"E25.filletArc");var subQ23=sQuery(id+"F0.wireOp",EDGE,"E26.filletArc");var subQ24=sQuery(id+"F0.wireOp",EDGE,"E27.filletArc");var subQ25=sQuery(id+"F0.wireOp",EDGE,"E28.filletArc");var subQ26=sQuery(id+"F0.wireOp",EDGE,"E29.filletArc");var subQ27=sQuery(id+"F0.wireOp",EDGE,"E31");var subQ28=sQuery(id+"F0.wireOp",EDGE,"E32");var subQ29=sQuery(id+"F0.wireOp",EDGE,"E33.filletArc");var subQ30=sQuery(id+"F0.wireOp",EDGE,"E34.filletArc");var subQ31=sQuery(id+"F0.wireOp",EDGE,"E35");var subQ32=sQuery(id+"F0.wireOp",EDGE,"E36");var subQ33=sQuery(id+"F0.wireOp",EDGE,"E37");var subQ34=sQuery(id+"F0.wireOp",EDGE,"E38");Q0=makeQuery(id+"F3.boolean.opBoolean","SPLIT",FACE,{"disambiguationData":[TD([makeQuery(id+"F1.opExtrude","SWEPT_FACE",FACE,{"disambiguationData":[OSD([subQ15])]})])],"derivedFrom":makeQuery(id+"F1.opExtrude","CAP_FACE",FACE,{"disambiguationData":[OSD([subQ15,subQ12,subQ11,subQ13,subQ17,subQ18,subQ19,subQ20,subQ21,subQ16,subQ10,subQ9,subQ8,subQ7,subQ6,subQ5,subQ4,subQ3,subQ2,subQ1,subQ0,subQ14,subQ22,subQ23,subQ24,subQ25,subQ26,subQ27,subQ28,subQ29,subQ30,subQ31,subQ32,subQ33,subQ34])],"isStart":true})});}
            var Q1;
            Q1=makeQuery(id+"F3.boolean.opBoolean","COPY",FACE,{"derivedFrom":makeQuery(id+"F3.opRevolve","SWEPT_FACE",FACE,{"disambiguationData":[OSD([sQuery(id+"F2.wireOp",EDGE,"E41")])]})});
            var Q2;
            Q2=makeQuery(id+"F3.boolean.opBoolean","SPLIT",FACE,{"disambiguationData":[TD([makeQuery(id+"F3.opRevolve","SWEPT_FACE",FACE,{"disambiguationData":[OSD([sQuery(id+"F2.wireOp",EDGE,"E40")])]})])],"derivedFrom":makeQuery(id+"F1.opExtrude","CAP_FACE",FACE,{"disambiguationData":[OSD([sQuery(id+"F0.wireOp",EDGE,"E1"),sQuery(id+"F0.wireOp",EDGE,"E3"),sQuery(id+"F0.wireOp",EDGE,"E4"),sQuery(id+"F0.wireOp",EDGE,"E5"),sQuery(id+"F0.wireOp",EDGE,"E6"),sQuery(id+"F0.wireOp",EDGE,"E7"),sQuery(id+"F0.wireOp",EDGE,"E8.trimOffspring"),sQuery(id+"F0.wireOp",EDGE,"E9.trimOffspring"),sQuery(id+"F0.wireOp",EDGE,"E10.trimOffspring"),sQuery(id+"F0.wireOp",EDGE,"E11.trimOffspring"),sQuery(id+"F0.wireOp",EDGE,"E12.trimOffspring"),sQuery(id+"F0.wireOp",EDGE,"E13"),sQuery(id+"F0.wireOp",EDGE,"E14"),sQuery(id+"F0.wireOp",EDGE,"E15"),sQuery(id+"F0.wireOp",EDGE,"E16"),sQuery(id+"F0.wireOp",EDGE,"E17"),sQuery(id+"F0.wireOp",EDGE,"E19"),sQuery(id+"F0.wireOp",EDGE,"E20"),sQuery(id+"F0.wireOp",EDGE,"E21.filletArc"),sQuery(id+"F0.wireOp",EDGE,"E22.filletArc"),sQuery(id+"F0.wireOp",EDGE,"E23.filletArc"),sQuery(id+"F0.wireOp",EDGE,"E24.filletArc"),sQuery(id+"F0.wireOp",EDGE,"E25.filletArc"),sQuery(id+"F0.wireOp",EDGE,"E26.filletArc"),sQuery(id+"F0.wireOp",EDGE,"E27.filletArc"),sQuery(id+"F0.wireOp",EDGE,"E28.filletArc"),sQuery(id+"F0.wireOp",EDGE,"E29.filletArc"),sQuery(id+"F0.wireOp",EDGE,"E31"),sQuery(id+"F0.wireOp",EDGE,"E32"),sQuery(id+"F0.wireOp",EDGE,"E33.filletArc"),sQuery(id+"F0.wireOp",EDGE,"E34.filletArc"),sQuery(id+"F0.wireOp",EDGE,"E35"),sQuery(id+"F0.wireOp",EDGE,"E36"),sQuery(id+"F0.wireOp",EDGE,"E37"),sQuery(id+"F0.wireOp",EDGE,"E38")])],"isStart":true})});
            var Q3;
            Q3=makeQuery(id+"F3.boolean.opBoolean","COPY",FACE,{"derivedFrom":makeQuery(id+"F3.opRevolve","SWEPT_FACE",FACE,{"disambiguationData":[OSD([sQuery(id+"F2.wireOp",EDGE,"E45.right")])]})});
            var Q4;
            Q4=makeQuery(id+"F1.opExtrude","CAP_FACE",FACE,{"disambiguationData":[OSD([sQuery(id+"F0.wireOp",EDGE,"E1"),sQuery(id+"F0.wireOp",EDGE,"E3"),sQuery(id+"F0.wireOp",EDGE,"E4"),sQuery(id+"F0.wireOp",EDGE,"E5"),sQuery(id+"F0.wireOp",EDGE,"E6"),sQuery(id+"F0.wireOp",EDGE,"E7"),sQuery(id+"F0.wireOp",EDGE,"E8.trimOffspring"),sQuery(id+"F0.wireOp",EDGE,"E9.trimOffspring"),sQuery(id+"F0.wireOp",EDGE,"E10.trimOffspring"),sQuery(id+"F0.wireOp",EDGE,"E11.trimOffspring"),sQuery(id+"F0.wireOp",EDGE,"E12.trimOffspring"),sQuery(id+"F0.wireOp",EDGE,"E13"),sQuery(id+"F0.wireOp",EDGE,"E14"),sQuery(id+"F0.wireOp",EDGE,"E15"),sQuery(id+"F0.wireOp",EDGE,"E16"),sQuery(id+"F0.wireOp",EDGE,"E17"),sQuery(id+"F0.wireOp",EDGE,"E19"),sQuery(id+"F0.wireOp",EDGE,"E20"),sQuery(id+"F0.wireOp",EDGE,"E21.filletArc"),sQuery(id+"F0.wireOp",EDGE,"E22.filletArc"),sQuery(id+"F0.wireOp",EDGE,"E23.filletArc"),sQuery(id+"F0.wireOp",EDGE,"E24.filletArc"),sQuery(id+"F0.wireOp",EDGE,"E25.filletArc"),sQuery(id+"F0.wireOp",EDGE,"E26.filletArc"),sQuery(id+"F0.wireOp",EDGE,"E27.filletArc"),sQuery(id+"F0.wireOp",EDGE,"E28.filletArc"),sQuery(id+"F0.wireOp",EDGE,"E29.filletArc"),sQuery(id+"F0.wireOp",EDGE,"E31"),sQuery(id+"F0.wireOp",EDGE,"E32"),sQuery(id+"F0.wireOp",EDGE,"E33.filletArc"),sQuery(id+"F0.wireOp",EDGE,"E34.filletArc"),sQuery(id+"F0.wireOp",EDGE,"E35"),sQuery(id+"F0.wireOp",EDGE,"E36"),sQuery(id+"F0.wireOp",EDGE,"E37"),sQuery(id+"F0.wireOp",EDGE,"E38")])],"isStart":false});
            var Q5;
            Q5=makeQuery(id+"F1.opExtrude","SWEPT_FACE",FACE,{"disambiguationData":[OSD([sQuery(id+"F0.wireOp",EDGE,"E37")])]});
            var Q6;
            Q6=makeQuery(id+"F1.opExtrude","SWEPT_FACE",FACE,{"disambiguationData":[OSD([sQuery(id+"F0.wireOp",EDGE,"E13")])]});
            var Q7;
            Q7=makeQuery(id+"F1.opExtrude","SWEPT_FACE",FACE,{"disambiguationData":[OSD([sQuery(id+"F0.wireOp",EDGE,"E15")])]});
            fillet(context, id + "F18", {"entities" : qUnion([Q0, Q1, Q2, Q3, Q4, Q5, Q6, Q7]), "radius" : 0.2 * mm, "tangentPropagation" : true, "allowEdgeOverflow" : false});
        }
        {
            var Q0;
            Q0=makeQuery(id+"F17.boolean.opBoolean","INTERSECT",EDGE,{"derivedFrom":[makeQuery(id+"F3.boolean.opBoolean","COPY",FACE,{"derivedFrom":makeQuery(id+"F3.opRevolve","SWEPT_FACE",FACE,{"disambiguationData":[OSD([sQuery(id+"F2.wireOp",EDGE,"E40")])]})}),makeQuery(id+"F17.opExtrude","SWEPT_FACE",FACE,{"disambiguationData":[OSD([sQuery(id+"F14.wireOp",EDGE,"E66")])]})]});
            fillet(context, id + "F19", {"entities" : qUnion([Q0]), "radius" : 0.2 * mm, "tangentPropagation" : true, "allowEdgeOverflow" : false});
        }
    });
